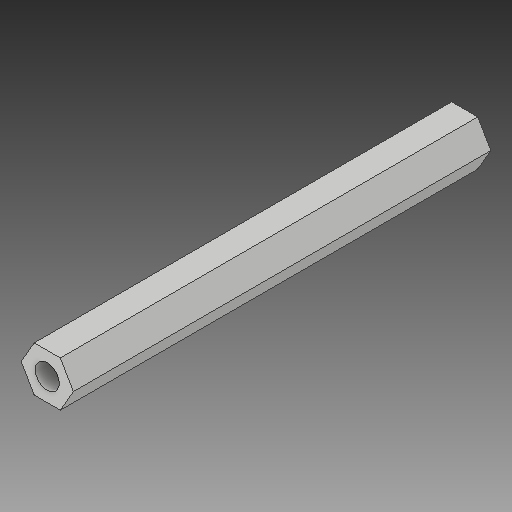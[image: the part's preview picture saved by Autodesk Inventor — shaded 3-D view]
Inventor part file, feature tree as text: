
AUTODESK INVENTOR PART (.ipt)
format: ipt  version: 2017 (Build 210142000, 142)  size: 104,960 bytes
history: native  units: in
note: dims shown in document units (in); Inventor stores cm internally (conversion verified against a paired STEP export)
features: other x3, sketch x1
ambient origin geometry x8: Origin, YZ Plane, XZ Plane, XY Plane, X Axis, Y Axis, Z Axis, Center Point
bodies: Solid1 (feature_tree)
feature tree (4):
  other  "Front_Wheel_Hex_Shaft.ipt"
  other  "Solid1::Front_Wheel_Hex_Shaft.ipt"
  other  "TaggingFeature1"
  sketch  "Sketch1"  dims[d0=0.3937in]
